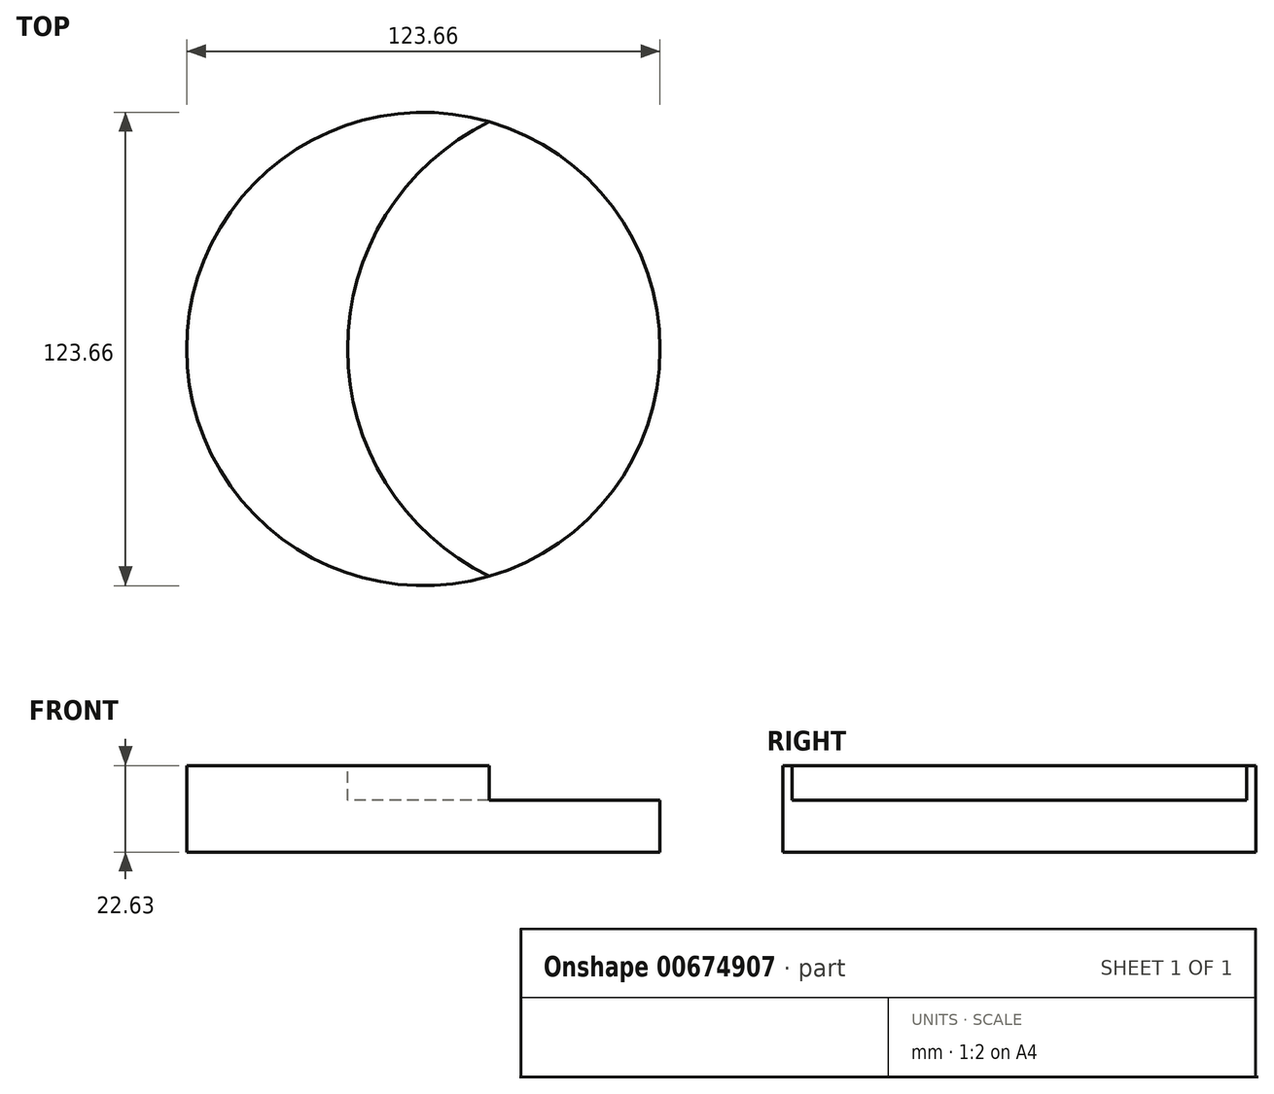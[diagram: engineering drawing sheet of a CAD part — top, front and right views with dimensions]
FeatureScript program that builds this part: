
annotation { "Feature Type Name" : "Feature", "Feature Type Description" : "" }
export const myFeature = defineFeature(function(context is Context, id is Id, definition is map)
    precondition{}
    {
        {
            var Q0;
            Q0=qCreatedBy(makeId("Top.planeOp"),FACE);
            var sketch = newSketch(context, id + "F0", { "sketchPlane" : qUnion([Q0])});
            skCircle(sketch, "E0", {"center": v(0, 0) * mm, "radius": 61.83 * mm});
            skSolve(sketch);
        }
        {
            var Q0;
            Q0=makeQuery(id+"F0.imprint","IMPRINT",FACE,{"disambiguationData":[TD([[makeQuery(id+"F0.imprint","IMPRINT",EDGE,{"derivedFrom":sQuery(id+"F0.wireOp",EDGE,"E0")}),1.0]])]});
            extrude(context, id + "F1", {"entities" : qUnion([Q0]), "depth" : 22.63 * mm, "offsetDistance" : 25.4 * mm});
        }
        {
            var Q0;
            Q0=makeQuery(id+"F1.opExtrude","CAP_FACE",FACE,{"disambiguationData":[OSD([sQuery(id+"F0.wireOp",EDGE,"E0")])],"isStart":false});
            var sketch = newSketch(context, id + "F2", { "sketchPlane" : qUnion([Q0])});
            skCircle(sketch, "E1", {"center": v(46.34, 0) * mm, "radius": 66.17 * mm});
            skSolve(sketch);
        }
        {
            var Q0;
            {var subQ0=sQuery(id+"F2.wireOp",EDGE,"E1");var subQ1=makeQuery(id+"F1.opExtrude","CAP_EDGE",EDGE,{"disambiguationData":[OSD([sQuery(id+"F0.wireOp",EDGE,"E0")])],"isStart":false});var subQ2=makeQuery(id+"F2.imprint","INTERSECT",VERTEX,{"disambiguationData":[OD(0.0)],"derivedFrom":[subQ1,subQ0]});Q0=makeQuery(id+"F2.imprint","IMPRINT",FACE,{"disambiguationData":[TD([[makeQuery(id+"F2.imprint","IMPRINT",EDGE,{"disambiguationData":[TD([[subQ2,1.0]])],"derivedFrom":subQ0}),1.0]])]});}
            var Q1;
            Q1 = qSketchRegion(id + "F2", true);
            extrude(context, id + "F3", {"entities" : qUnion([Q0, Q1]), "operationType" : NewBodyOperationType.REMOVE, "oppositeDirection" : true, "depth" : 9.1 * mm, "offsetDistance" : 25.4 * mm});
        }
    });
